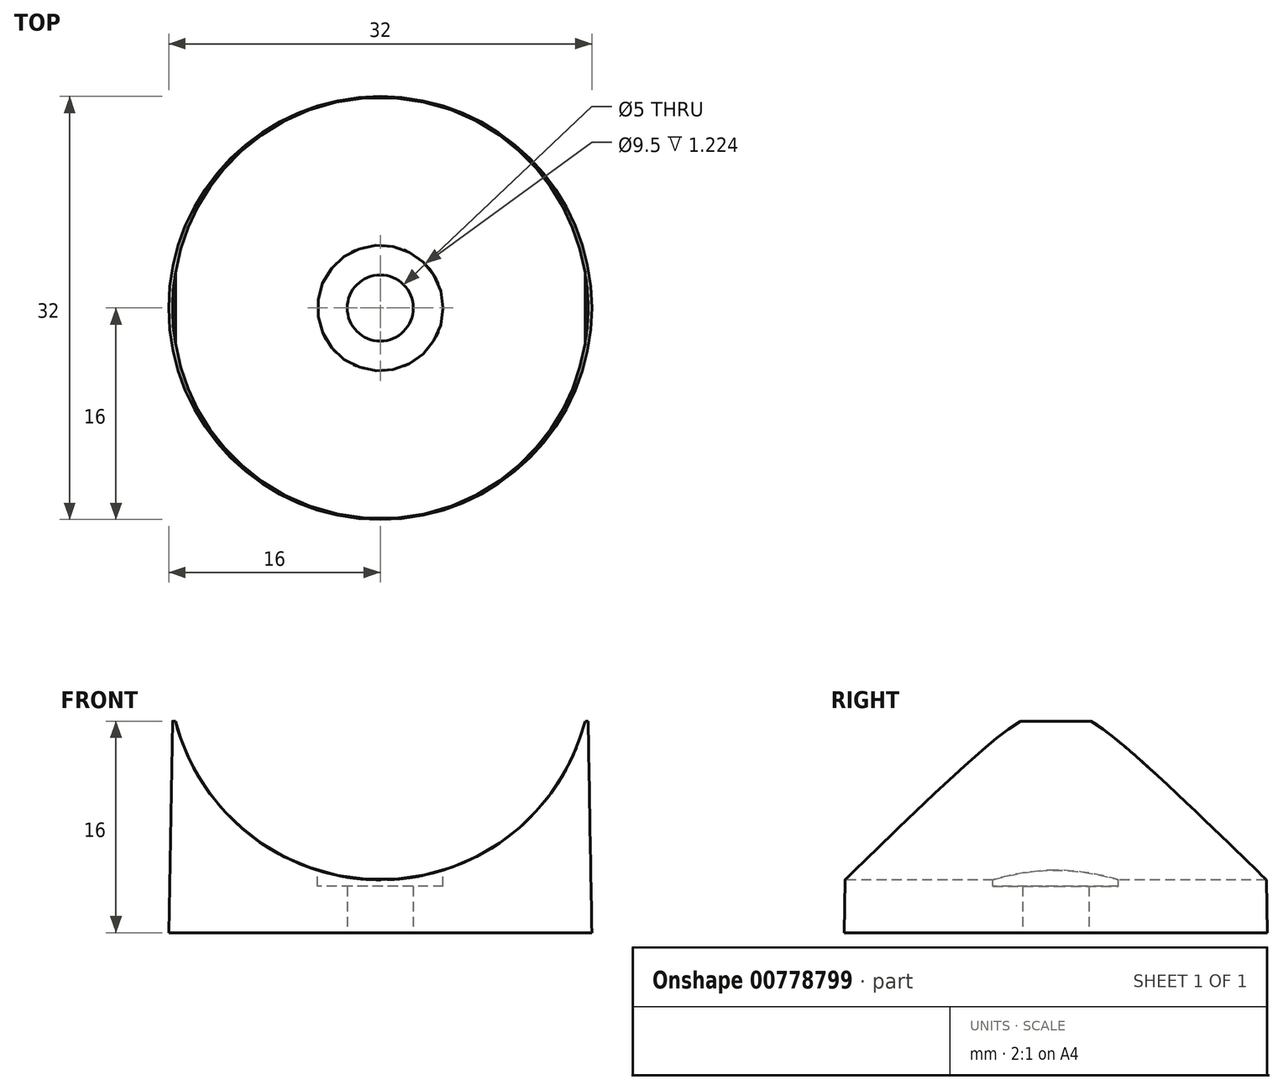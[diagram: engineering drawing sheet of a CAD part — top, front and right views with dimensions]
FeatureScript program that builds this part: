
annotation { "Feature Type Name" : "Feature", "Feature Type Description" : "" }
export const myFeature = defineFeature(function(context is Context, id is Id, definition is map)
    precondition{}
    {
        {
            var Q0;
            Q0=qCreatedBy(makeId("Top.planeOp"),FACE);
            var sketch = newSketch(context, id + "F0", { "sketchPlane" : qUnion([Q0])});
            skCircle(sketch, "E0", {"center": v(0, 0) * mm, "radius": 16 * mm});
            skSolve(sketch);
        }
        {
            var Q0;
            Q0 = qSketchRegion(id + "F0", true);
            extrude(context, id + "F1", {"entities" : qUnion([Q0]), "depth" : 16 * mm, "offsetDistance" : 25 * mm, "hasDraft" : true, "draftAngle" : 1 * degree, "draftPullDirection" : true});
        }
        {
            var Q0;
            Q0=qCreatedBy(makeId("Front.planeOp"),FACE);
            var sketch = newSketch(context, id + "F2", { "sketchPlane" : qUnion([Q0])});
            skCircle(sketch, "E1", {"center": v(0, 20) * mm, "radius": 16 * mm});
            skSolve(sketch);
        }
        {
            var Q0;
            Q0 = qSketchRegion(id + "F2", true);
            extrude(context, id + "F3", {"entities" : qUnion([Q0]), "operationType" : NewBodyOperationType.REMOVE, "oppositeDirection" : true, "depth" : 32 * mm, "offsetDistance" : 25 * mm, "symmetric" : true});
        }
        {
            var Q0;
            Q0=makeQuery(id+"F1.opExtrude","CAP_FACE",FACE,{"disambiguationData":[OSD([sQuery(id+"F0.wireOp",EDGE,"E0")])],"isStart":true});
            var sketch = newSketch(context, id + "F4", { "sketchPlane" : qUnion([Q0])});
            skCircle(sketch, "E2", {"center": v(0, 0) * mm, "radius": 2.5 * mm});
            skSolve(sketch);
        }
        {
            var Q0;
            Q0 = qSketchRegion(id + "F4", true);
            extrude(context, id + "F5", {"entities" : qUnion([Q0]), "operationType" : NewBodyOperationType.REMOVE, "oppositeDirection" : true, "depth" : 5 * mm, "offsetDistance" : 25 * mm});
        }
        {
            var Q0;
            Q0=qCreatedBy(makeId("Top.planeOp"),FACE);
            cPlane(context, id + "F6", {"entities" : qUnion([Q0]), "cplaneType" : CPlaneType.OFFSET, "offset" : 5 * mm, "width" : 150 * mm, "height" : 150 * mm});
        }
        {
            var Q0;
            Q0=qCreatedBy(id+"F6.planeOp",FACE);
            var sketch = newSketch(context, id + "F7", { "sketchPlane" : qUnion([Q0])});
            skCircle(sketch, "E3", {"center": v(0, 0) * mm, "radius": 4.75 * mm});
            skSolve(sketch);
        }
        {
            var Q0;
            Q0 = qSketchRegion(id + "F7", true);
            extrude(context, id + "F8", {"entities" : qUnion([Q0]), "operationType" : NewBodyOperationType.REMOVE, "oppositeDirection" : true, "depth" : 1.5 * mm, "offsetDistance" : 25 * mm});
        }
    });
